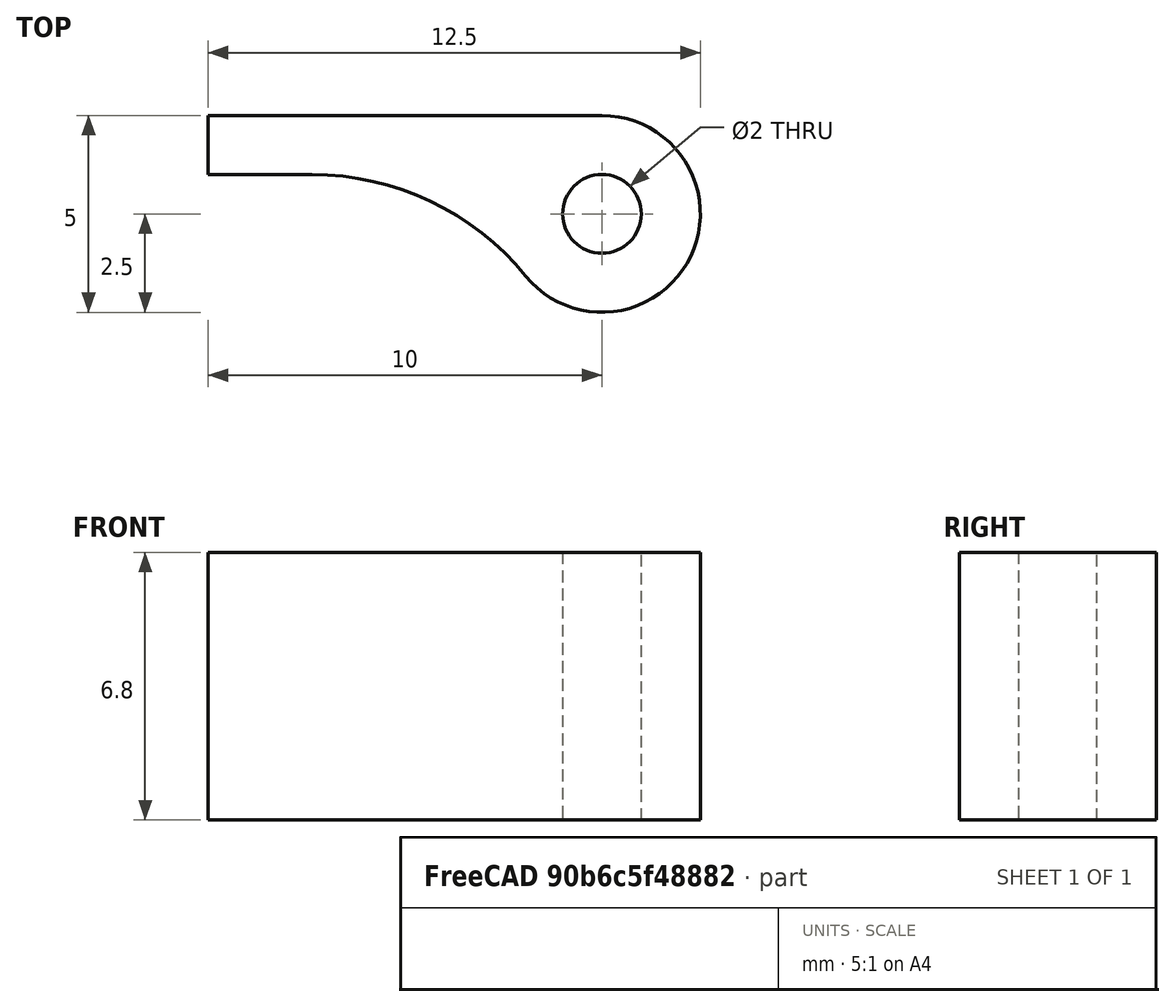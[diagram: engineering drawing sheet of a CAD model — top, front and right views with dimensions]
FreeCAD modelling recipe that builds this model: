
FCSTD DOCUMENT  (FreeCAD 0.16R6712 (Git))
Label: SecurityPinClip
License: All rights reserved
LicenseURL: http://en.wikipedia.org/wiki/All_rights_reserved
objects: Sketcher::SketchObject×1, PartDesign::Pad×1
note: 3 computed .brp shape members not serialized (recipe doc carries the construction recipe); baked Part::Feature solids carry a one-line shape summary decoded from their .brp

FEATURE [Sketcher::SketchObject] Sketch
  sketch-geometry (6):
    g0: Circle CenterX=0 CenterY=0 CenterZ=0 NormalX=0 NormalY=0 NormalZ=1 Radius=1
    g1: LineSegment StartX=0 StartY=2.5 StartZ=0 EndX=-10 EndY=2.5 EndZ=0
    g2: ArcOfCircle CenterX=0 CenterY=0 CenterZ=0 NormalX=0 NormalY=0 NormalZ=1 Radius=2.5 StartAngle=3.82518 EndAngle=7.85398
    g3: ArcOfCircle CenterX=-7.36546 CenterY=-6 CenterZ=0 NormalX=0 NormalY=0 NormalZ=1 Radius=7 StartAngle=0.683589 EndAngle=1.57079
    g4: LineSegment StartX=-7.36543 StartY=1 StartZ=0 EndX=-10 EndY=1 EndZ=0
    g5: LineSegment StartX=-10 StartY=2.5 StartZ=0 EndX=-10 EndY=1 EndZ=0
  constraints (18):
    c: Coincident(g0,g-1)
    c: Radius(g0) = 1
    c: PointOnObject(g1,g-2)
    c: Horizontal(g1)
    c: Coincident(g2,g-1)
    c: Coincident(g2,g1)
    c: Coincident(g3,g2)
    c: Coincident(g4,g3)
    c: Horizontal(g4)
    c: Coincident(g5,g1)
    c: Coincident(g5,g4)
    c: Vertical(g5)
    c: Tangent(g3,g4)
    c: Tangent(g2,g3)
    c: Distance(g5) = 1.5
    c: Radius(g2) = 2.5
    c: Distance(g1) = 10
    c: Radius(g3) = 7
FEATURE [PartDesign::Pad] Pad
  Length = 6.8
  Length2 = 100
  Sketch = -> Sketch
  Type = 0
